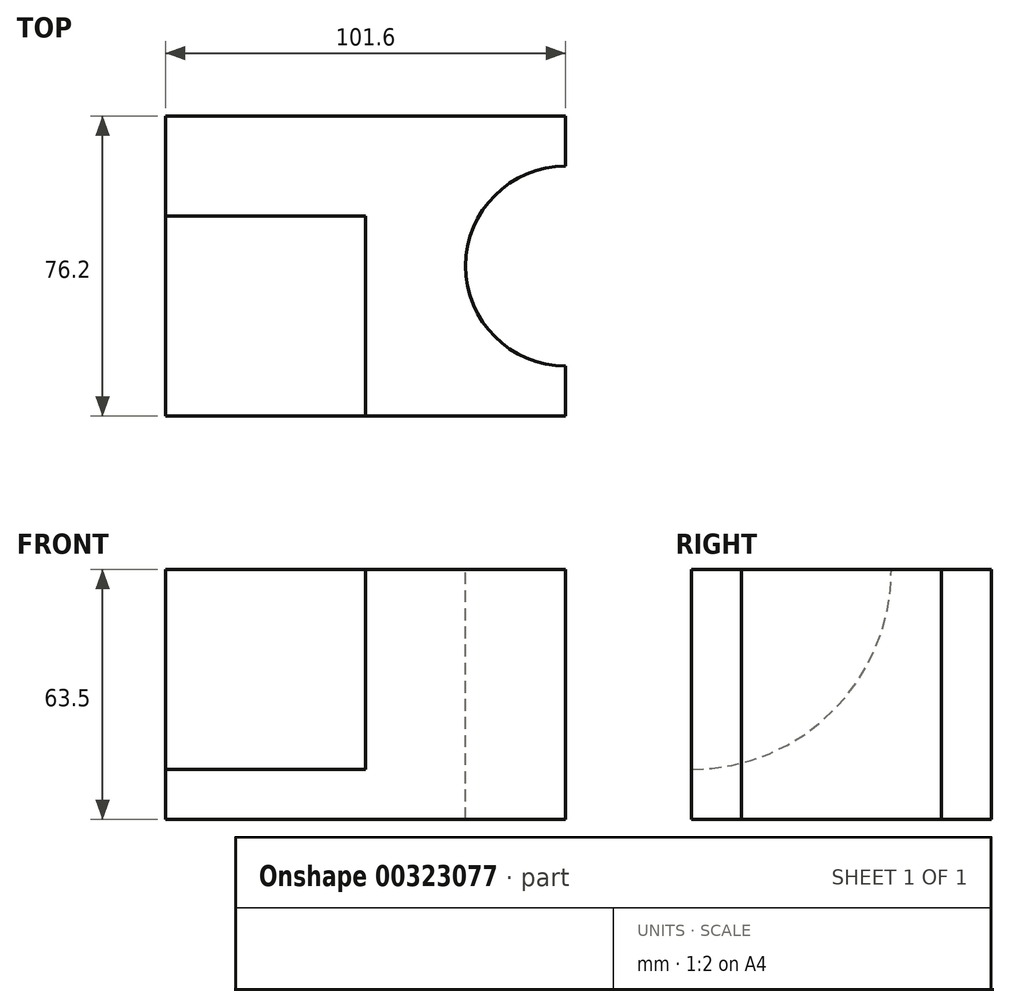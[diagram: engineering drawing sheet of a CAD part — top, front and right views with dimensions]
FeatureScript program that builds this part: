
annotation { "Feature Type Name" : "Feature", "Feature Type Description" : "" }
export const myFeature = defineFeature(function(context is Context, id is Id, definition is map)
    precondition{}
    {
        {
            var Q0;
            Q0=qCreatedBy(makeId("Front.planeOp"),FACE);
            var sketch = newSketch(context, id + "F0", { "sketchPlane" : qUnion([Q0])});
            skLineSegment(sketch, "E0", {"start": v(-30.11, 31.75) * mm, "end": v(-30.11, -31.75) * mm});
            skLineSegment(sketch, "E1", {"start": v(-30.11, -31.75) * mm, "end": v(71.49, -31.75) * mm});
            skLineSegment(sketch, "E2", {"start": v(71.49, -31.75) * mm, "end": v(71.49, 31.75) * mm});
            skLineSegment(sketch, "E3", {"start": v(71.49, 31.75) * mm, "end": v(-30.11, 31.75) * mm});
            skSolve(sketch);
        }
        {
            var Q0;
            Q0=makeQuery(id+"F0.imprint","IMPRINT",FACE,{"disambiguationData":[TD([[makeQuery(id+"F0.imprint","IMPRINT",EDGE,{"derivedFrom":sQuery(id+"F0.wireOp",EDGE,"E0")}),1.0]])]});
            extrude(context, id + "F1", {"entities" : qUnion([Q0]), "depth" : 76.2 * mm});
        }
        {
            var Q0;
            Q0=makeQuery(id+"F1.opExtrude","SWEPT_FACE",FACE,{"disambiguationData":[OSD([sQuery(id+"F0.wireOp",EDGE,"E3")])]});
            var sketch = newSketch(context, id + "F2", { "sketchPlane" : qUnion([Q0])});
            skArc(sketch, "E4", {"start": v(71.49, -12.7) * mm, "mid": v(46.09, -38.1) * mm, "end": v(71.49, -63.5) * mm});
            skLineSegment(sketch, "E5", {"start": v(71.49, -63.5) * mm, "end": v(71.49, -12.7) * mm});
            skSolve(sketch);
        }
        {
            var Q0;
            Q0=makeQuery(id+"F2.imprint","IMPRINT",FACE,{"disambiguationData":[TD([[makeQuery(id+"F2.imprint","IMPRINT",EDGE,{"derivedFrom":sQuery(id+"F2.wireOp",EDGE,"E4")}),1.0]])]});
            extrude(context, id + "F3", {"entities" : qUnion([Q0]), "operationType" : NewBodyOperationType.REMOVE, "endBound" : BoundingType.THROUGH_ALL, "oppositeDirection" : true, "depth" : 25.4 * mm});
        }
        {
            var Q0;
            Q0=makeQuery(id+"F1.opExtrude","SWEPT_FACE",FACE,{"disambiguationData":[OSD([sQuery(id+"F0.wireOp",EDGE,"E0")])]});
            var sketch = newSketch(context, id + "F4", { "sketchPlane" : qUnion([Q0])});
            skArc(sketch, "E6", {"start": v(25.4, 31.75) * mm, "mid": v(40.28, -4.17) * mm, "end": v(76.2, -19.05) * mm});
            skLineSegment(sketch, "E7", {"start": v(25.4, 31.75) * mm, "end": v(76.2, 31.75) * mm});
            skLineSegment(sketch, "E8", {"start": v(76.2, -19.05) * mm, "end": v(76.2, 31.75) * mm});
            skSolve(sketch);
        }
        {
            var Q0;
            Q0=makeQuery(id+"F4.imprint","IMPRINT",FACE,{"disambiguationData":[TD([[makeQuery(id+"F4.imprint","IMPRINT",EDGE,{"derivedFrom":sQuery(id+"F4.wireOp",EDGE,"E6")}),1.0]])]});
            extrude(context, id + "F5", {"entities" : qUnion([Q0]), "operationType" : NewBodyOperationType.REMOVE, "oppositeDirection" : true, "depth" : 50.8 * mm});
        }
    });
